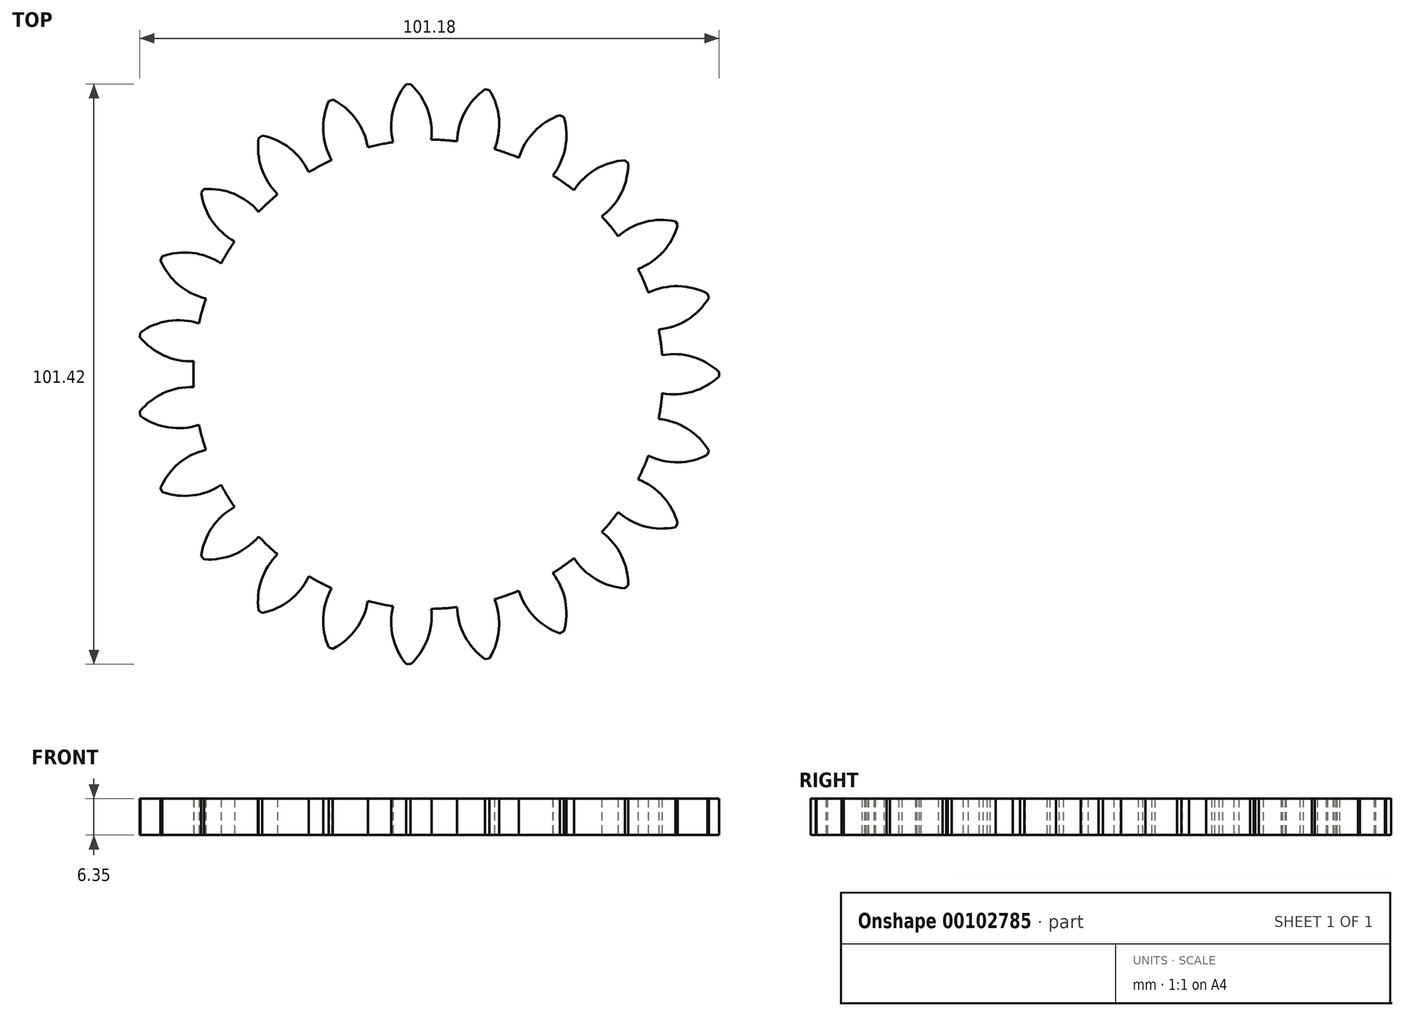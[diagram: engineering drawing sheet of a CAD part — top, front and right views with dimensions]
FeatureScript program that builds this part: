
annotation { "Feature Type Name" : "Feature", "Feature Type Description" : "" }
export const myFeature = defineFeature(function(context is Context, id is Id, definition is map)
    precondition{}
    {
        {
            var Q0;
            Q0=qCreatedBy(makeId("Top.planeOp"),FACE);
            var sketch = newSketch(context, id + "F0", { "sketchPlane" : qUnion([Q0])});
            skCircle(sketch, "E0", {"center": v(0, 0) * mm, "radius": 41.02 * mm});
            skCircle(sketch, "E1", {"center": v(0, 0) * mm, "radius": 45.97 * mm, "construction": true});
            skCircle(sketch, "E2", {"center": v(0, 0) * mm, "radius": 50.8 * mm, "construction": true});
            skLineSegment(sketch, "E3", {"start": v(0, 0) * mm, "end": v(0, 79.15) * mm, "construction": true});
            skLineSegment(sketch, "E4", {"start": v(0, 0) * mm, "end": v(-5.97, 87.28) * mm, "construction": true});
            skLineSegment(sketch, "E5", {"start": v(0, 45.97) * mm, "end": v(-60.46, 25.38) * mm, "construction": true});
            skLineSegment(sketch, "E6", {"start": v(0, 45.97) * mm, "end": v(-65.99, 47.35) * mm, "construction": true});
            skCircle(sketch, "E7", {"center": v(0, 45.97) * mm, "radius": 11.5 * mm, "construction": true});
            skArc(sketch, "E8", {"start": v(-3.08, 50.7) * mm, "mid": v(-21.65, 38.24) * mm, "end": v(0.55, 41.02) * mm, "construction": true});
            skArc(sketch, "E9", {"start": v(0.55, 41.02) * mm, "mid": v(-0.11, 46.3) * mm, "end": v(-3.08, 50.7) * mm});
            skArc(sketch, "E10.MirrorCS", {"start": v(-6.12, 40.56) * mm, "mid": v(-6.19, 45.88) * mm, "end": v(-3.85, 50.65) * mm});
            skArc(sketch, "E11.1.0", {"start": v(-10.54, 39.64) * mm, "mid": v(-12.6, 44.55) * mm, "end": v(-16.64, 48) * mm});
            skArc(sketch, "E11.1.1", {"start": v(-16.84, 37.4) * mm, "mid": v(-18.33, 42.5) * mm, "end": v(-17.38, 47.74) * mm});
            skArc(sketch, "E11.2.0", {"start": v(-20.85, 35.33) * mm, "mid": v(-24.15, 39.5) * mm, "end": v(-28.97, 41.73) * mm});
            skArc(sketch, "E11.2.1", {"start": v(-26.3, 31.48) * mm, "mid": v(-29.12, 35.98) * mm, "end": v(-29.6, 41.28) * mm});
            skArc(sketch, "E11.3.0", {"start": v(-29.6, 28.4) * mm, "mid": v(-33.9, 31.51) * mm, "end": v(-39.16, 32.36) * mm});
            skArc(sketch, "E11.3.1", {"start": v(-33.82, 23.21) * mm, "mid": v(-37.75, 26.8) * mm, "end": v(-39.65, 31.76) * mm});
            skArc(sketch, "E11.4.0", {"start": v(-36.17, 19.35) * mm, "mid": v(-41.15, 21.2) * mm, "end": v(-46.44, 20.6) * mm});
            skArc(sketch, "E11.4.1", {"start": v(-38.83, 13.23) * mm, "mid": v(-43.58, 15.61) * mm, "end": v(-46.75, 19.88) * mm});
            skArc(sketch, "E11.5.0", {"start": v(-40.05, 8.88) * mm, "mid": v(-45.35, 9.3) * mm, "end": v(-50.27, 7.3) * mm});
            skArc(sketch, "E11.5.1", {"start": v(-40.96, 2.26) * mm, "mid": v(-46.18, 3.28) * mm, "end": v(-50.38, 6.53) * mm});
            skArc(sketch, "E11.6.0", {"start": v(-40.96, -2.26) * mm, "mid": v(-46.18, -3.27) * mm, "end": v(-50.38, -6.53) * mm});
            skArc(sketch, "E11.6.1", {"start": v(-40.05, -8.87) * mm, "mid": v(-45.35, -9.3) * mm, "end": v(-50.27, -7.3) * mm});
            skArc(sketch, "E11.7.0", {"start": v(-38.83, -13.22) * mm, "mid": v(-43.58, -15.6) * mm, "end": v(-46.75, -19.88) * mm});
            skArc(sketch, "E11.7.1", {"start": v(-36.17, -19.35) * mm, "mid": v(-41.16, -21.2) * mm, "end": v(-46.44, -20.6) * mm});
            skArc(sketch, "E11.8.0", {"start": v(-33.82, -23.2) * mm, "mid": v(-37.75, -26.79) * mm, "end": v(-39.65, -31.75) * mm});
            skArc(sketch, "E11.8.1", {"start": v(-29.6, -28.4) * mm, "mid": v(-33.91, -31.51) * mm, "end": v(-39.16, -32.36) * mm});
            skArc(sketch, "E11.9.0", {"start": v(-26.3, -31.47) * mm, "mid": v(-29.13, -35.98) * mm, "end": v(-29.61, -41.28) * mm});
            skArc(sketch, "E11.9.1", {"start": v(-20.85, -35.33) * mm, "mid": v(-24.15, -39.5) * mm, "end": v(-28.98, -41.72) * mm});
            skArc(sketch, "E11.10.0", {"start": v(-16.84, -37.4) * mm, "mid": v(-18.34, -42.5) * mm, "end": v(-17.38, -47.73) * mm});
            skArc(sketch, "E11.10.1", {"start": v(-10.55, -39.64) * mm, "mid": v(-12.6, -44.54) * mm, "end": v(-16.65, -48) * mm});
            skArc(sketch, "E11.11.0", {"start": v(-6.13, -40.56) * mm, "mid": v(-6.2, -45.88) * mm, "end": v(-3.86, -50.65) * mm});
            skArc(sketch, "E11.11.1", {"start": v(0.54, -41.02) * mm, "mid": v(-0.12, -46.3) * mm, "end": v(-3.08, -50.7) * mm});
            skArc(sketch, "E11.12.0", {"start": v(5.04, -40.7) * mm, "mid": v(6.42, -45.85) * mm, "end": v(9.95, -49.82) * mm});
            skArc(sketch, "E11.12.1", {"start": v(11.59, -39.35) * mm, "mid": v(12.38, -44.6) * mm, "end": v(10.71, -49.66) * mm});
            skArc(sketch, "E11.13.0", {"start": v(15.84, -37.84) * mm, "mid": v(18.55, -42.41) * mm, "end": v(23.02, -45.28) * mm});
            skArc(sketch, "E11.13.1", {"start": v(21.77, -34.76) * mm, "mid": v(23.95, -39.61) * mm, "end": v(23.71, -44.93) * mm});
            skArc(sketch, "E11.14.0", {"start": v(25.46, -32.16) * mm, "mid": v(29.3, -35.84) * mm, "end": v(34.39, -37.4) * mm});
            skArc(sketch, "E11.14.1", {"start": v(30.35, -27.6) * mm, "mid": v(33.75, -31.68) * mm, "end": v(34.95, -36.86) * mm});
            skArc(sketch, "E11.15.0", {"start": v(33.2, -24.1) * mm, "mid": v(37.89, -26.6) * mm, "end": v(43.2, -26.73) * mm});
            skArc(sketch, "E11.15.1", {"start": v(36.67, -18.4) * mm, "mid": v(41.05, -21.4) * mm, "end": v(43.6, -26.06) * mm});
            skArc(sketch, "E11.16.0", {"start": v(38.47, -14.25) * mm, "mid": v(43.66, -15.4) * mm, "end": v(48.8, -14.08) * mm});
            skArc(sketch, "E11.16.1", {"start": v(40.27, -7.82) * mm, "mid": v(45.3, -9.53) * mm, "end": v(49.02, -13.33) * mm});
            skArc(sketch, "E11.17.0", {"start": v(40.88, -3.34) * mm, "mid": v(46.2, -3.05) * mm, "end": v(50.8, -0.4) * mm});
            skArc(sketch, "E11.17.1", {"start": v(40.88, 3.34) * mm, "mid": v(46.2, 3.04) * mm, "end": v(50.8, 0.39) * mm});
            skArc(sketch, "E11.18.0", {"start": v(40.27, 7.81) * mm, "mid": v(45.3, 9.53) * mm, "end": v(49.02, 13.33) * mm});
            skArc(sketch, "E11.18.1", {"start": v(38.47, 14.25) * mm, "mid": v(43.66, 15.4) * mm, "end": v(48.81, 14.08) * mm});
            skArc(sketch, "E11.19.0", {"start": v(36.67, 18.39) * mm, "mid": v(41.05, 21.4) * mm, "end": v(43.6, 26.06) * mm});
            skArc(sketch, "E11.19.1", {"start": v(33.2, 24.1) * mm, "mid": v(37.89, 26.6) * mm, "end": v(43.2, 26.72) * mm});
            skArc(sketch, "E11.20.0", {"start": v(30.35, 27.6) * mm, "mid": v(33.75, 31.68) * mm, "end": v(34.96, 36.86) * mm});
            skArc(sketch, "E11.20.1", {"start": v(25.47, 32.16) * mm, "mid": v(29.3, 35.83) * mm, "end": v(34.4, 37.39) * mm});
            skArc(sketch, "E11.21.0", {"start": v(21.78, 34.76) * mm, "mid": v(23.96, 39.61) * mm, "end": v(23.72, 44.92) * mm});
            skArc(sketch, "E11.21.1", {"start": v(15.85, 37.84) * mm, "mid": v(18.55, 42.41) * mm, "end": v(23.03, 45.28) * mm});
            skArc(sketch, "E11.22.0", {"start": v(11.6, 39.35) * mm, "mid": v(12.38, 44.6) * mm, "end": v(10.72, 49.66) * mm});
            skArc(sketch, "E11.22.1", {"start": v(5.05, 40.7) * mm, "mid": v(6.42, 45.85) * mm, "end": v(9.96, 49.81) * mm});
            skPoint(sketch, "E12", {"position": v(-3.46, 50.68) * mm});
            skPoint(sketch, "E13", {"position": v(10.41, 49.72) * mm});
            skLineSegment(sketch, "E14", {"start": v(-3.85, 50.65) * mm, "end": v(-3.08, 50.7) * mm});
            skLineSegment(sketch, "E15.1.0", {"start": v(-17.38, 47.74) * mm, "end": v(-16.64, 48) * mm});
            skLineSegment(sketch, "E15.2.0", {"start": v(-29.6, 41.28) * mm, "end": v(-28.97, 41.73) * mm});
            skLineSegment(sketch, "E15.3.0", {"start": v(-39.65, 31.76) * mm, "end": v(-39.16, 32.36) * mm});
            skLineSegment(sketch, "E15.4.0", {"start": v(-46.75, 19.88) * mm, "end": v(-46.44, 20.6) * mm});
            skLineSegment(sketch, "E15.5.0", {"start": v(-50.38, 6.53) * mm, "end": v(-50.27, 7.3) * mm});
            skLineSegment(sketch, "E15.6.0", {"start": v(-50.27, -7.3) * mm, "end": v(-50.38, -6.53) * mm});
            skLineSegment(sketch, "E15.7.0", {"start": v(-46.44, -20.6) * mm, "end": v(-46.75, -19.88) * mm});
            skLineSegment(sketch, "E15.8.0", {"start": v(-39.16, -32.36) * mm, "end": v(-39.65, -31.75) * mm});
            skLineSegment(sketch, "E15.9.0", {"start": v(-28.98, -41.72) * mm, "end": v(-29.61, -41.28) * mm});
            skLineSegment(sketch, "E15.10.0", {"start": v(-16.65, -48) * mm, "end": v(-17.38, -47.73) * mm});
            skLineSegment(sketch, "E15.11.0", {"start": v(-3.08, -50.7) * mm, "end": v(-3.86, -50.65) * mm});
            skLineSegment(sketch, "E15.12.0", {"start": v(10.71, -49.66) * mm, "end": v(9.95, -49.82) * mm});
            skLineSegment(sketch, "E15.13.0", {"start": v(23.71, -44.93) * mm, "end": v(23.02, -45.28) * mm});
            skLineSegment(sketch, "E15.14.0", {"start": v(34.95, -36.86) * mm, "end": v(34.39, -37.4) * mm});
            skLineSegment(sketch, "E15.15.0", {"start": v(43.6, -26.06) * mm, "end": v(43.2, -26.73) * mm});
            skLineSegment(sketch, "E15.16.0", {"start": v(49.02, -13.33) * mm, "end": v(48.8, -14.08) * mm});
            skLineSegment(sketch, "E15.17.0", {"start": v(50.8, 0.39) * mm, "end": v(50.8, -0.4) * mm});
            skLineSegment(sketch, "E15.18.0", {"start": v(48.81, 14.08) * mm, "end": v(49.02, 13.33) * mm});
            skLineSegment(sketch, "E15.19.0", {"start": v(43.2, 26.72) * mm, "end": v(43.6, 26.06) * mm});
            skLineSegment(sketch, "E15.20.0", {"start": v(34.4, 37.39) * mm, "end": v(34.96, 36.86) * mm});
            skLineSegment(sketch, "E15.21.0", {"start": v(23.03, 45.28) * mm, "end": v(23.72, 44.92) * mm});
            skLineSegment(sketch, "E15.22.0", {"start": v(9.96, 49.81) * mm, "end": v(10.72, 49.66) * mm});
            skSolve(sketch);
        }
        {
            var Q0;
            Q0 = qSketchRegion(id + "F0", true);
            extrude(context, id + "F1", {"entities" : qUnion([Q0]), "depth" : 6.35 * mm});
        }
    });
